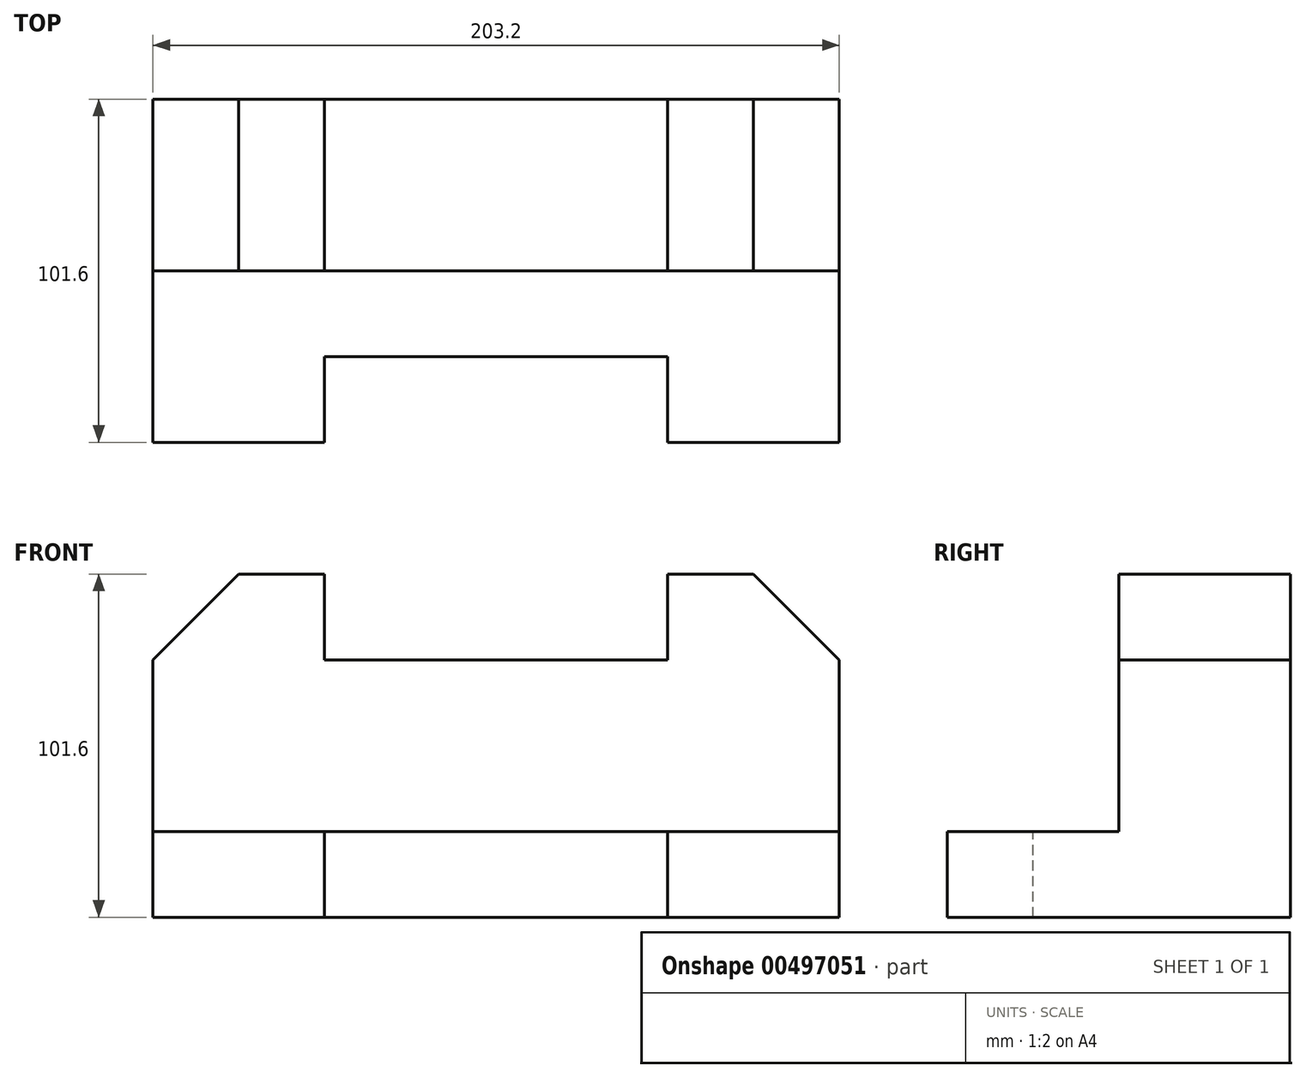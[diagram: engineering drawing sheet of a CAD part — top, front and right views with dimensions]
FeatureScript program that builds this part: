
annotation { "Feature Type Name" : "Feature", "Feature Type Description" : "" }
export const myFeature = defineFeature(function(context is Context, id is Id, definition is map)
    precondition{}
    {
        {
            var Q0;
            Q0=qCreatedBy(makeId("Front.planeOp"),FACE);
            var sketch = newSketch(context, id + "F0", { "sketchPlane" : qUnion([Q0])});
            skLineSegment(sketch, "E0", {"start": v(-71.77, -33.17) * mm, "end": v(-71.77, -7.77) * mm});
            skLineSegment(sketch, "E1", {"start": v(-71.77, -7.77) * mm, "end": v(131.43, -7.77) * mm});
            skLineSegment(sketch, "E2", {"start": v(131.43, -7.77) * mm, "end": v(131.43, -33.17) * mm});
            skLineSegment(sketch, "E3", {"start": v(131.43, -33.17) * mm, "end": v(-71.77, -33.17) * mm});
            skSolve(sketch);
        }
        {
            var Q0;
            Q0=makeQuery(id+"F0.imprint","IMPRINT",FACE,{"disambiguationData":[TD([[makeQuery(id+"F0.imprint","IMPRINT",EDGE,{"derivedFrom":sQuery(id+"F0.wireOp",EDGE,"E0")}),-1.0]])]});
            extrude(context, id + "F1", {"entities" : qUnion([Q0]), "depth" : 101.6 * mm});
        }
        {
            var Q0;
            Q0=makeQuery(id+"F1.opExtrude","SWEPT_FACE",FACE,{"disambiguationData":[OSD([sQuery(id+"F0.wireOp",EDGE,"E1")])]});
            var sketch = newSketch(context, id + "F2", { "sketchPlane" : qUnion([Q0])});
            skLineSegment(sketch, "E4", {"start": v(-71.77, -101.6) * mm, "end": v(-20.97, -101.6) * mm});
            skLineSegment(sketch, "E5", {"start": v(-20.97, -101.6) * mm, "end": v(-20.97, -76.2) * mm});
            skLineSegment(sketch, "E6", {"start": v(-20.97, -76.2) * mm, "end": v(80.63, -76.2) * mm});
            skLineSegment(sketch, "E7", {"start": v(80.63, -76.2) * mm, "end": v(80.63, -101.6) * mm});
            skLineSegment(sketch, "E8", {"start": v(80.63, -101.6) * mm, "end": v(131.43, -101.6) * mm});
            skLineSegment(sketch, "E9", {"start": v(-20.97, -101.6) * mm, "end": v(80.63, -101.6) * mm});
            skSolve(sketch);
        }
        {
            var Q0;
            Q0=makeQuery(id+"F2.imprint","IMPRINT",FACE,{"disambiguationData":[TD([[makeQuery(id+"F2.imprint","IMPRINT",EDGE,{"derivedFrom":sQuery(id+"F2.wireOp",EDGE,"E5")}),-1.0]])]});
            extrude(context, id + "F3", {"entities" : qUnion([Q0]), "operationType" : NewBodyOperationType.REMOVE, "oppositeDirection" : true, "depth" : 25.4 * mm});
        }
        {
            var Q0;
            Q0=makeQuery(id+"F1.opExtrude","SWEPT_FACE",FACE,{"disambiguationData":[OSD([sQuery(id+"F0.wireOp",EDGE,"E2")])]});
            var sketch = newSketch(context, id + "F4", { "sketchPlane" : qUnion([Q0])});
            skLineSegment(sketch, "E10", {"start": v(0, -7.77) * mm, "end": v(0, 43.03) * mm});
            skLineSegment(sketch, "E11", {"start": v(0, 43.03) * mm, "end": v(-50.8, 43.03) * mm});
            skLineSegment(sketch, "E12", {"start": v(-50.8, 43.03) * mm, "end": v(-50.8, -7.77) * mm});
            skSolve(sketch);
        }
        {
            var Q0;
            {var subQ0=sQuery(id+"F4.wireOp",EDGE,"E10");Q0=makeQuery(id+"F4.imprint","IMPRINT",FACE,{"disambiguationData":[TD([[makeQuery(id+"F4.imprint","IMPRINT",EDGE,{"derivedFrom":subQ0}),1.0]])]});}
            extrude(context, id + "F5", {"entities" : qUnion([Q0]), "operationType" : NewBodyOperationType.ADD, "depth" : -203.2 * mm});
        }
        {
            var Q0;
            Q0=makeQuery(id+"F5.opExtrude","SWEPT_FACE",FACE,{"disambiguationData":[OSD([sQuery(id+"F4.wireOp",EDGE,"E11")])]});
            var sketch = newSketch(context, id + "F6", { "sketchPlane" : qUnion([Q0])});
            skLineSegment(sketch, "E13", {"start": v(-71.77, -50.8) * mm, "end": v(-20.97, -50.8) * mm});
            skLineSegment(sketch, "E14", {"start": v(-20.97, -50.8) * mm, "end": v(-20.97, 0) * mm});
            skLineSegment(sketch, "E15", {"start": v(-20.97, 0) * mm, "end": v(-71.77, 0) * mm});
            skLineSegment(sketch, "E16", {"start": v(-71.77, 0) * mm, "end": v(-71.77, -50.8) * mm});
            skLineSegment(sketch, "E17", {"start": v(131.43, -50.8) * mm, "end": v(80.63, -50.8) * mm});
            skLineSegment(sketch, "E18", {"start": v(80.63, -50.8) * mm, "end": v(80.63, 0) * mm});
            skLineSegment(sketch, "E19", {"start": v(80.63, 0) * mm, "end": v(131.43, 0) * mm});
            skLineSegment(sketch, "E20", {"start": v(131.43, 0) * mm, "end": v(131.43, -50.8) * mm});
            skSolve(sketch);
        }
        {
            var Q0;
            Q0=makeQuery(id+"F6.imprint","IMPRINT",FACE,{"disambiguationData":[TD([[makeQuery(id+"F6.imprint","IMPRINT",EDGE,{"derivedFrom":sQuery(id+"F6.wireOp",EDGE,"E13")}),1.0]])]});
            var Q1;
            Q1=makeQuery(id+"F6.imprint","IMPRINT",FACE,{"disambiguationData":[TD([[makeQuery(id+"F6.imprint","IMPRINT",EDGE,{"derivedFrom":sQuery(id+"F6.wireOp",EDGE,"E17")}),1.0]])]});
            extrude(context, id + "F7", {"entities" : qUnion([Q0, Q1]), "operationType" : NewBodyOperationType.ADD, "depth" : 25.4 * mm});
        }
        {
            var Q0;
            Q0=makeQuery(id+"F7.boolean.opBoolean","MERGE",FACE,{"derivedFrom":[makeQuery(id+"F5.opExtrude","SWEPT_FACE",FACE,{"disambiguationData":[OSD([sQuery(id+"F4.wireOp",EDGE,"E12")])]}),makeQuery(id+"F7.opExtrude","SWEPT_FACE",FACE,{"disambiguationData":[OSD([sQuery(id+"F6.wireOp",EDGE,"E13")])]}),makeQuery(id+"F7.opExtrude","SWEPT_FACE",FACE,{"disambiguationData":[OSD([sQuery(id+"F6.wireOp",EDGE,"E17")])]})]});
            var sketch = newSketch(context, id + "F8", { "sketchPlane" : qUnion([Q0])});
            skLineSegment(sketch, "E21", {"start": v(-20.97, 68.43) * mm, "end": v(-46.37, 68.43) * mm});
            skLineSegment(sketch, "E22", {"start": v(-20.97, 43.03) * mm, "end": v(-71.77, 43.03) * mm});
            skLineSegment(sketch, "E23", {"start": v(-71.77, 43.03) * mm, "end": v(-46.37, 68.43) * mm});
            skLineSegment(sketch, "E24", {"start": v(80.63, 43.03) * mm, "end": v(131.43, 43.03) * mm});
            skLineSegment(sketch, "E25", {"start": v(80.63, 68.43) * mm, "end": v(106.03, 68.43) * mm});
            skLineSegment(sketch, "E26", {"start": v(106.03, 68.43) * mm, "end": v(131.43, 43.03) * mm});
            skLineSegment(sketch, "E27", {"start": v(-71.77, 43.03) * mm, "end": v(-71.77, 68.43) * mm});
            skLineSegment(sketch, "E28", {"start": v(-71.77, 68.43) * mm, "end": v(-46.37, 68.43) * mm});
            skLineSegment(sketch, "E29", {"start": v(106.03, 68.43) * mm, "end": v(131.43, 68.43) * mm});
            skLineSegment(sketch, "E30", {"start": v(131.43, 68.43) * mm, "end": v(131.43, 43.03) * mm});
            skSolve(sketch);
        }
        {
            var Q0;
            Q0=makeQuery(id+"F8.imprint","IMPRINT",FACE,{"disambiguationData":[TD([[makeQuery(id+"F8.imprint","IMPRINT",EDGE,{"derivedFrom":sQuery(id+"F8.wireOp",EDGE,"E26")}),1.0]])]});
            var Q1;
            Q1=makeQuery(id+"F8.imprint","IMPRINT",FACE,{"disambiguationData":[TD([[makeQuery(id+"F8.imprint","IMPRINT",EDGE,{"derivedFrom":sQuery(id+"F8.wireOp",EDGE,"E23")}),1.0]])]});
            extrude(context, id + "F9", {"entities" : qUnion([Q0, Q1]), "operationType" : NewBodyOperationType.REMOVE, "oppositeDirection" : true, "depth" : 50.8 * mm});
        }
    });
